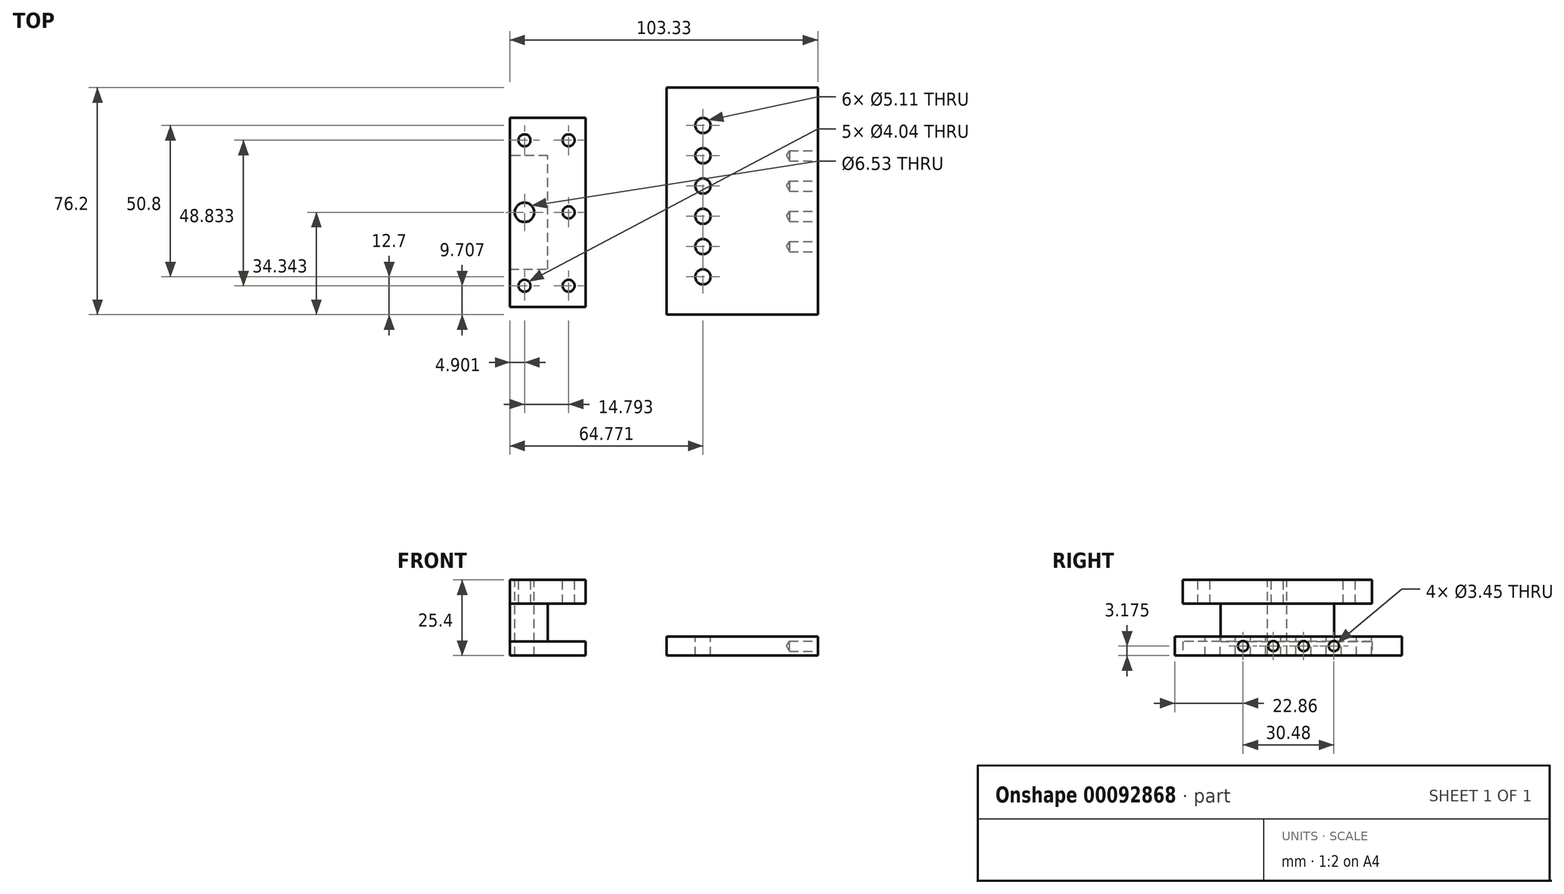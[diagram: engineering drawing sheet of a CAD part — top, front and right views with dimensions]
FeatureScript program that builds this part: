
annotation { "Feature Type Name" : "Feature", "Feature Type Description" : "" }
export const myFeature = defineFeature(function(context is Context, id is Id, definition is map)
    precondition{}
    {
        {
            var Q0;
            Q0=qCreatedBy(makeId("Top.planeOp"),FACE);
            var sketch = newSketch(context, id + "F0", { "sketchPlane" : qUnion([Q0])});
            skLineSegment(sketch, "E0.bottom", {"start": v(25.4, -38.1) * mm, "end": v(-25.4, -38.1) * mm});
            skLineSegment(sketch, "E0.top", {"start": v(25.4, 38.1) * mm, "end": v(-25.4, 38.1) * mm});
            skLineSegment(sketch, "E0.left", {"start": v(25.4, -38.1) * mm, "end": v(25.4, 38.1) * mm});
            skLineSegment(sketch, "E0.right", {"start": v(-25.4, -38.1) * mm, "end": v(-25.4, 38.1) * mm});
            skPoint(sketch, "E0.middle", {"position": v(0, 0) * mm});
            skSolve(sketch);
        }
        {
            var Q0;
            Q0=makeQuery(id+"F0.imprint","IMPRINT",FACE,{"disambiguationData":[TD([[makeQuery(id+"F0.imprint","IMPRINT",EDGE,{"derivedFrom":sQuery(id+"F0.wireOp",EDGE,"E0.bottom")}),-1.0]])]});
            extrude(context, id + "F1", {"entities" : qUnion([Q0]), "depth" : 6.35 * mm});
        }
        {
            var Q0;
            Q0=makeQuery(id+"F1.opExtrude","CAP_FACE",FACE,{"disambiguationData":[OSD([sQuery(id+"F0.wireOp",EDGE,"E0.bottom"),sQuery(id+"F0.wireOp",EDGE,"E0.top"),sQuery(id+"F0.wireOp",EDGE,"E0.left"),sQuery(id+"F0.wireOp",EDGE,"E0.right")])],"isStart":false});
            var sketch = newSketch(context, id + "F2", { "sketchPlane" : qUnion([Q0])});
            skLineSegment(sketch, "E1", {"start": v(-13.16, 38.1) * mm, "end": v(-13.16, -38.1) * mm, "construction": true});
            skLineSegment(sketch, "E2", {"start": v(-25.4, 25.4) * mm, "end": v(25.4, 25.4) * mm, "construction": true});
            skLineSegment(sketch, "E3", {"start": v(-25.4, 15.24) * mm, "end": v(25.4, 15.24) * mm, "construction": true});
            skLineSegment(sketch, "E4", {"start": v(-25.4, 5.08) * mm, "end": v(25.4, 5.08) * mm, "construction": true});
            skLineSegment(sketch, "E5", {"start": v(-25.4, -5.08) * mm, "end": v(25.4, -5.08) * mm, "construction": true});
            skLineSegment(sketch, "E6", {"start": v(-25.4, -15.24) * mm, "end": v(25.4, -15.24) * mm, "construction": true});
            skLineSegment(sketch, "E7", {"start": v(-25.4, -25.4) * mm, "end": v(25.4, -25.4) * mm, "construction": true});
            skPoint(sketch, "E8", {"position": v(-13.16, 25.4) * mm});
            skPoint(sketch, "E9", {"position": v(-13.16, 15.24) * mm});
            skPoint(sketch, "E10", {"position": v(-13.16, 5.08) * mm});
            skPoint(sketch, "E11", {"position": v(-13.16, -5.08) * mm});
            skPoint(sketch, "E12", {"position": v(-13.16, -15.24) * mm});
            skPoint(sketch, "E13", {"position": v(-13.16, -25.4) * mm});
            skSolve(sketch);
        }
        {
            var Q0;
            Q0=sQuery(id+"F2.wireOp",VERTEX,"E8");
            var Q1;
            Q1=sQuery(id+"F2.wireOp",VERTEX,"E9");
            var Q2;
            Q2=sQuery(id+"F2.wireOp",VERTEX,"E10");
            var Q3;
            Q3=sQuery(id+"F2.wireOp",VERTEX,"E11");
            var Q4;
            Q4=sQuery(id+"F2.wireOp",VERTEX,"E12");
            var Q5;
            Q5=sQuery(id+"F2.wireOp",VERTEX,"E13");
            var Q6;
            Q6=makeQuery(id+"F1.opExtrude","SWEPT_BODY",BODY,{"disambiguationData":[OSD([sQuery(id+"F0.wireOp",EDGE,"E0.bottom"),sQuery(id+"F0.wireOp",EDGE,"E0.top"),sQuery(id+"F0.wireOp",EDGE,"E0.left"),sQuery(id+"F0.wireOp",EDGE,"E0.right")])]});
            hole(context, id + "F3", {"style" : HoleStyle.SIMPLE, "endStyle" : HoleEndStyle.THROUGH, "standardTappedOrClearance" : lookupTablePath({ "standard" : "ANSI", "engagement" : "75%", "pitch" : "20 tpi", "size" : "1/4", "type" : "Tapped" }), "standardBlindInLast" : lookupTablePath({ "standard" : "ANSI", "engagement" : "75%", "pitch" : "20 tpi", "size" : "1/4", "type" : "Tapped" }), "holeDiameter" : 5.1 * mm, "locations" : qUnion([Q0, Q1, Q2, Q3, Q4, Q5]), "scope" : qUnion([Q6]), "isTappedThrough" : true, "majorDiameter" : 6.35 * mm, "showTappedDepth" : true});
        }
        {
            var Q0;
            Q0=makeQuery(id+"F1.opExtrude","SWEPT_FACE",FACE,{"disambiguationData":[OSD([sQuery(id+"F0.wireOp",EDGE,"E0.left")])]});
            var sketch = newSketch(context, id + "F4", { "sketchPlane" : qUnion([Q0])});
            skLineSegment(sketch, "E14.0.0", {"start": v(-38.1, 0) * mm, "end": v(38.1, 0) * mm, "construction": true});
            skLineSegment(sketch, "E14.0.1", {"start": v(38.1, 0) * mm, "end": v(38.1, 6.35) * mm, "construction": true});
            skLineSegment(sketch, "E14.0.2", {"start": v(38.1, 6.35) * mm, "end": v(-38.1, 6.35) * mm, "construction": true});
            skLineSegment(sketch, "E14.0.3", {"start": v(-38.1, 6.35) * mm, "end": v(-38.1, 0) * mm, "construction": true});
            skPoint(sketch, "E15.0", {"position": v(-15.24, 6.35) * mm});
            skPoint(sketch, "E16.0", {"position": v(-5.08, 6.35) * mm});
            skPoint(sketch, "E17.0", {"position": v(5.08, 6.35) * mm});
            skPoint(sketch, "E18.0", {"position": v(15.24, 6.35) * mm});
            skLineSegment(sketch, "E19", {"start": v(-15.24, 6.35) * mm, "end": v(-15.24, 0) * mm, "construction": true});
            skLineSegment(sketch, "E20", {"start": v(-5.08, 6.35) * mm, "end": v(-5.08, 0) * mm, "construction": true});
            skLineSegment(sketch, "E21", {"start": v(5.08, 6.35) * mm, "end": v(5.08, 0) * mm, "construction": true});
            skLineSegment(sketch, "E22", {"start": v(15.24, 6.35) * mm, "end": v(15.24, 0) * mm, "construction": true});
            skPoint(sketch, "E23", {"position": v(-15.24, 3.18) * mm});
            skPoint(sketch, "E24", {"position": v(-5.08, 3.18) * mm});
            skPoint(sketch, "E25", {"position": v(5.08, 3.18) * mm});
            skPoint(sketch, "E26", {"position": v(15.24, 3.18) * mm});
            skSolve(sketch);
        }
        {
            var Q0;
            Q0=sQuery(id+"F4.wireOp",VERTEX,"E23");
            var Q1;
            Q1=sQuery(id+"F4.wireOp",VERTEX,"E24");
            var Q2;
            Q2=sQuery(id+"F4.wireOp",VERTEX,"E25");
            var Q3;
            Q3=sQuery(id+"F4.wireOp",VERTEX,"E26");
            var Q4;
            Q4=makeQuery(id+"F1.opExtrude","SWEPT_BODY",BODY,{"disambiguationData":[OSD([sQuery(id+"F0.wireOp",EDGE,"E0.bottom"),sQuery(id+"F0.wireOp",EDGE,"E0.top"),sQuery(id+"F0.wireOp",EDGE,"E0.left"),sQuery(id+"F0.wireOp",EDGE,"E0.right")])]});
            hole(context, id + "F5", {"style" : HoleStyle.SIMPLE, "endStyle" : HoleEndStyle.BLIND, "standardTappedOrClearance" : lookupTablePath({ "standard" : "ANSI", "engagement" : "75%", "pitch" : "32 tpi", "size" : "#8", "type" : "Tapped" }), "standardBlindInLast" : lookupTablePath({ "standard" : "ANSI", "engagement" : "75%", "pitch" : "32 tpi", "size" : "#8", "type" : "Tapped" }), "holeDiameter" : 3.45 * mm, "holeDepth" : 9.52 * mm, "locations" : qUnion([Q0, Q1, Q2, Q3]), "scope" : qUnion([Q4]), "majorDiameter" : 4.17 * mm});
        }
        {
            var Q0;
            Q0=qCreatedBy(makeId("Top.planeOp"),FACE);
            var sketch = newSketch(context, id + "F6", { "sketchPlane" : qUnion([Q0])});
            skLineSegment(sketch, "E27.bottom", {"start": v(-77.93, 28) * mm, "end": v(-52.53, 28) * mm});
            skLineSegment(sketch, "E27.top", {"start": v(-77.93, -35.5) * mm, "end": v(-52.53, -35.5) * mm});
            skLineSegment(sketch, "E27.left", {"start": v(-77.93, 28) * mm, "end": v(-77.93, -35.5) * mm});
            skLineSegment(sketch, "E27.right", {"start": v(-52.53, 28) * mm, "end": v(-52.53, -35.5) * mm});
            skSolve(sketch);
        }
        {
            var Q0;
            Q0=makeQuery(id+"F6.imprint","IMPRINT",FACE,{"disambiguationData":[TD([[makeQuery(id+"F6.imprint","IMPRINT",EDGE,{"derivedFrom":sQuery(id+"F6.wireOp",EDGE,"E27.bottom")}),-1.0]])]});
            extrude(context, id + "F7", {"entities" : qUnion([Q0]), "depth" : 25.4 * mm});
        }
        {
            var Q0;
            Q0=makeQuery(id+"F7.opExtrude","SWEPT_FACE",FACE,{"disambiguationData":[OSD([sQuery(id+"F6.wireOp",EDGE,"E27.top")])]});
            var sketch = newSketch(context, id + "F8", { "sketchPlane" : qUnion([Q0])});
            skLineSegment(sketch, "E28", {"start": v(-77.93, 4.75) * mm, "end": v(-52.53, 4.75) * mm});
            skLineSegment(sketch, "E29", {"start": v(-77.93, 17.48) * mm, "end": v(-52.53, 17.48) * mm});
            skLineSegment(sketch, "E30", {"start": v(-77.93, 17.48) * mm, "end": v(-77.93, 4.75) * mm});
            skLineSegment(sketch, "E31", {"start": v(-52.53, 17.48) * mm, "end": v(-52.53, 4.75) * mm});
            skSolve(sketch);
        }
        {
            var Q0;
            Q0=makeQuery(id+"F8.imprint","IMPRINT",FACE,{"disambiguationData":[TD([[makeQuery(id+"F8.imprint","IMPRINT",EDGE,{"derivedFrom":sQuery(id+"F8.wireOp",EDGE,"E28")}),1.0]])]});
            extrude(context, id + "F9", {"entities" : qUnion([Q0]), "operationType" : NewBodyOperationType.REMOVE, "oppositeDirection" : true, "depth" : 12.7 * mm});
        }
        {
            var Q0;
            Q0=makeQuery(id+"F7.opExtrude","SWEPT_FACE",FACE,{"disambiguationData":[OSD([sQuery(id+"F6.wireOp",EDGE,"E27.bottom")])]});
            var sketch = newSketch(context, id + "F10", { "sketchPlane" : qUnion([Q0])});
            skLineSegment(sketch, "E32", {"start": v(52.53, 17.48) * mm, "end": v(77.93, 17.48) * mm});
            skLineSegment(sketch, "E33", {"start": v(52.53, 4.75) * mm, "end": v(77.93, 4.75) * mm});
            skLineSegment(sketch, "E34", {"start": v(52.53, 17.48) * mm, "end": v(52.53, 4.75) * mm});
            skLineSegment(sketch, "E35", {"start": v(77.93, 17.48) * mm, "end": v(77.93, 4.75) * mm});
            skSolve(sketch);
        }
        {
            var Q0;
            Q0=makeQuery(id+"F10.imprint","IMPRINT",FACE,{"disambiguationData":[TD([[makeQuery(id+"F10.imprint","IMPRINT",EDGE,{"derivedFrom":sQuery(id+"F10.wireOp",EDGE,"E32")}),-1.0]])]});
            extrude(context, id + "F11", {"entities" : qUnion([Q0]), "operationType" : NewBodyOperationType.REMOVE, "oppositeDirection" : true, "depth" : 12.7 * mm});
        }
        {
            var Q0;
            Q0=makeQuery(id+"F7.opExtrude","SWEPT_FACE",FACE,{"disambiguationData":[OSD([sQuery(id+"F6.wireOp",EDGE,"E27.right")])]});
            var sketch = newSketch(context, id + "F12", { "sketchPlane" : qUnion([Q0])});
            skLineSegment(sketch, "E36.0.0", {"start": v(15.3, 4.75) * mm, "end": v(15.3, 17.48) * mm});
            skLineSegment(sketch, "E36.0.1", {"start": v(15.3, 17.48) * mm, "end": v(28, 17.48) * mm});
            skLineSegment(sketch, "E36.0.2", {"start": v(28, 17.48) * mm, "end": v(28, 25.4) * mm});
            skLineSegment(sketch, "E36.0.3", {"start": v(28, 25.4) * mm, "end": v(-35.5, 25.4) * mm});
            skLineSegment(sketch, "E36.0.4", {"start": v(-35.5, 25.4) * mm, "end": v(-35.5, 17.48) * mm});
            skLineSegment(sketch, "E36.0.5", {"start": v(-35.5, 17.48) * mm, "end": v(-22.8, 17.48) * mm});
            skLineSegment(sketch, "E36.0.6", {"start": v(-22.8, 17.48) * mm, "end": v(-22.8, 4.75) * mm});
            skLineSegment(sketch, "E36.0.7", {"start": v(-22.8, 4.75) * mm, "end": v(-35.5, 4.75) * mm});
            skLineSegment(sketch, "E36.0.8", {"start": v(-35.5, 4.75) * mm, "end": v(-35.5, 0) * mm});
            skLineSegment(sketch, "E36.0.9", {"start": v(-35.5, 0) * mm, "end": v(28, 0) * mm});
            skLineSegment(sketch, "E36.0.10", {"start": v(28, 0) * mm, "end": v(28, 4.75) * mm});
            skLineSegment(sketch, "E36.0.11", {"start": v(28, 4.75) * mm, "end": v(15.3, 4.75) * mm});
            skLineSegment(sketch, "E37", {"start": v(-22.8, 4.75) * mm, "end": v(15.3, 4.75) * mm});
            skLineSegment(sketch, "E38", {"start": v(15.3, 17.48) * mm, "end": v(-22.8, 17.48) * mm});
            skSolve(sketch);
        }
        {
            var Q0;
            Q0=makeQuery(id+"F12.imprint","IMPRINT",FACE,{"disambiguationData":[TD([[makeQuery(id+"F12.imprint","IMPRINT",EDGE,{"derivedFrom":sQuery(id+"F12.wireOp",EDGE,"E36.0.6")}),1.0]])]});
            extrude(context, id + "F13", {"entities" : qUnion([Q0]), "operationType" : NewBodyOperationType.REMOVE, "oppositeDirection" : true, "depth" : 12.7 * mm});
        }
        {
            var Q0;
            Q0=makeQuery(id+"F7.opExtrude","CAP_FACE",FACE,{"disambiguationData":[OSD([sQuery(id+"F6.wireOp",EDGE,"E27.bottom"),sQuery(id+"F6.wireOp",EDGE,"E27.top"),sQuery(id+"F6.wireOp",EDGE,"E27.left"),sQuery(id+"F6.wireOp",EDGE,"E27.right")])],"isStart":false});
            var sketch = newSketch(context, id + "F14", { "sketchPlane" : qUnion([Q0])});
            skLineSegment(sketch, "E39", {"start": v(-77.93, 20.44) * mm, "end": v(-52.53, 20.44) * mm, "construction": true});
            skLineSegment(sketch, "E40", {"start": v(-77.93, -28.4) * mm, "end": v(-52.53, -28.4) * mm, "construction": true});
            skLineSegment(sketch, "E41", {"start": v(-58.24, 28) * mm, "end": v(-58.24, -35.5) * mm, "construction": true});
            skLineSegment(sketch, "E42", {"start": v(-73.03, 28) * mm, "end": v(-73.03, -35.5) * mm, "construction": true});
            skLineSegment(sketch, "E43", {"start": v(-77.93, -3.76) * mm, "end": v(-52.53, -3.76) * mm, "construction": true});
            skPoint(sketch, "E44", {"position": v(-73.03, 20.44) * mm});
            skPoint(sketch, "E45", {"position": v(-58.24, 20.44) * mm});
            skPoint(sketch, "E46", {"position": v(-73.03, -3.76) * mm});
            skPoint(sketch, "E47", {"position": v(-58.24, -3.76) * mm});
            skPoint(sketch, "E48", {"position": v(-58.24, -28.4) * mm});
            skPoint(sketch, "E49", {"position": v(-73.03, -28.4) * mm});
            skSolve(sketch);
        }
        {
            var Q0;
            Q0=sQuery(id+"F14.wireOp",VERTEX,"E44");
            var Q1;
            Q1=sQuery(id+"F14.wireOp",VERTEX,"E45");
            var Q2;
            Q2=sQuery(id+"F14.wireOp",VERTEX,"E47");
            var Q3;
            Q3=sQuery(id+"F14.wireOp",VERTEX,"E48");
            var Q4;
            Q4=sQuery(id+"F14.wireOp",VERTEX,"E49");
            var Q5;
            Q5=makeQuery(id+"F7.opExtrude","SWEPT_BODY",BODY,{"disambiguationData":[OSD([sQuery(id+"F6.wireOp",EDGE,"E27.bottom"),sQuery(id+"F6.wireOp",EDGE,"E27.top"),sQuery(id+"F6.wireOp",EDGE,"E27.left"),sQuery(id+"F6.wireOp",EDGE,"E27.right")])]});
            hole(context, id + "F15", {"style" : HoleStyle.SIMPLE, "endStyle" : HoleEndStyle.BLIND, "standardTappedOrClearance" : lookupTablePath({ "standard" : "ANSI", "engagement" : "75%", "pitch" : "32 tpi", "size" : "#10", "type" : "Tapped" }), "standardBlindInLast" : lookupTablePath({ "standard" : "ANSI", "engagement" : "75%", "pitch" : "32 tpi", "size" : "#10", "type" : "Tapped" }), "holeDiameter" : 4.04 * mm, "holeDepth" : 9.52 * mm, "locations" : qUnion([Q0, Q1, Q2, Q3, Q4]), "scope" : qUnion([Q5]), "majorDiameter" : 4.83 * mm});
        }
        {
            var Q0;
            Q0=sQuery(id+"F14.wireOp",VERTEX,"E46");
            var Q1;
            Q1=makeQuery(id+"F7.opExtrude","SWEPT_BODY",BODY,{"disambiguationData":[OSD([sQuery(id+"F6.wireOp",EDGE,"E27.bottom"),sQuery(id+"F6.wireOp",EDGE,"E27.top"),sQuery(id+"F6.wireOp",EDGE,"E27.left"),sQuery(id+"F6.wireOp",EDGE,"E27.right")])]});
            hole(context, id + "F16", {"style" : HoleStyle.SIMPLE, "endStyle" : HoleEndStyle.THROUGH, "standardTappedOrClearance" : lookupTablePath({ "standard" : "ANSI", "fit" : "Close", "size" : "1/4", "type" : "Clearance" }), "standardBlindInLast" : lookupTablePath({ "fit" : "Close", "standard" : "ANSI", "size" : "1/4", "type" : "Clearance" }), "holeDiameter" : 6.53 * mm, "locations" : qUnion([Q0]), "scope" : qUnion([Q1]), "isTappedThrough" : true});
        }
    });
